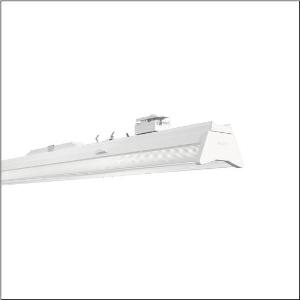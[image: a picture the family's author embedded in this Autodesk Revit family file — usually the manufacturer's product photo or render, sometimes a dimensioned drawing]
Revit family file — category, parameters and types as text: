
# Revit family: licross_r__21_performance_mo_52td16cn49xg_b518
name_source: partatom
category: Lighting Fixtures
units: mm (PartAtom-declared; Revit-internal decimal feet)

## family parameters
Cut with Voids When Loaded = No
Host = Face
Light Source = No
Part Type = Normal
Room Calculation Point = No
Round Connector Dimension = Use Diameter
Shared = No

## types (1)
- --- (1 x LED, 9240 lm, 50.4 W, 4000K)
    Apparent Load = 50 VA
    CIE Flux Codes = 66 88 96 79 100
    Color Rendering = 80
    Color Temperature = 4000K
    Default Elevation = 1800 mm
    Description = Licross® 21 Performance MO, luminaire insert, of sheet steel, galvanised, coil coated, white, length: 1.500mm, width: 120mm, height: 123mm, LED rated luminous flux: 9.240lm, light colour: 840, control gear: ON/OFF Multilumen, CLOi, control gear: ECG Multilumen, with plug, 3-pole, with phase selection, mains connection: 220..240V, AC, 50/60Hz, start of lifetime: 50W, end of service life: 61W, halogen-free wiring, primary light control with lens, of plastic, primary optical cover: cover, of PMMA, light emission: direct/indirect distribution, primary light characteristic: symmetric, protection rating (complete): IP54, insulation class (complete): insulation class I (protective earthing), certification: CE, ENEC, UKCA, protection symbol: D if used in an environment with non-conductive dust loads with corresponding accessories, impact resistance: IK06, permissible ambient temperature for indoor applications: -35..+45°C, corresponds to IFS (International Featured Standards) requirements for safety and quality in the food industry, reducing of maximum allowable ambient temperature of 5°C with ceiling mounting, LABS conformity tested according to VDMA 24364:2018-05, packaging unit: 1 piece
    Height = 114 mm
    Lamp = 1 x LED
    Lamp Light Flux = 9240 lm
    Lamp Power = 50.4 W
    Lamp count = 1
    Length = 1500 mm
    Luminous efficacy = 183 lm/W
    Manufacturer = Siteco
    ModVariant = No
    Model = 52TD16CN49XG
    Mounting Place = Ceiling
    Mounting Type = Pendant
    Number of Poles = 1
    OnlyDefault = Yes
    Power Factor = 1
    Product Name = Licross® 21 Performance MO
    Product group = luminaire insert
    ProductGroupID = 901
    Protection Class = Protection class I
    Protection Degree = IP 54
    RLX_Detail_Level = 1
    RLX_Emergency_Light_Flux = 0 lm
    RLX_Emergency_Type = 0
    RLX_Emergency_Type_DB = No
    RlxData = <blob elided: 31917 chars, md5=c1212a15>
    Socket = socket
    Standby Power = 0 W
    System Light Flux = 9240 lm
    System Power = 50 W
    Type Comments = factory setting: luminous flux: 100 % | (A | C | E) | 117 mA
    Type Image = l_1256138.jpg
    URL = http://relux.com
    VarID = @adj_080413
    Voltage = 0 V
    Weight = 0.00 kg
    Width = 120 mm

## geometry (parser evidence)
native form markers: Blend x4, Sweep x10
no freeform markers — native parametric forms only
